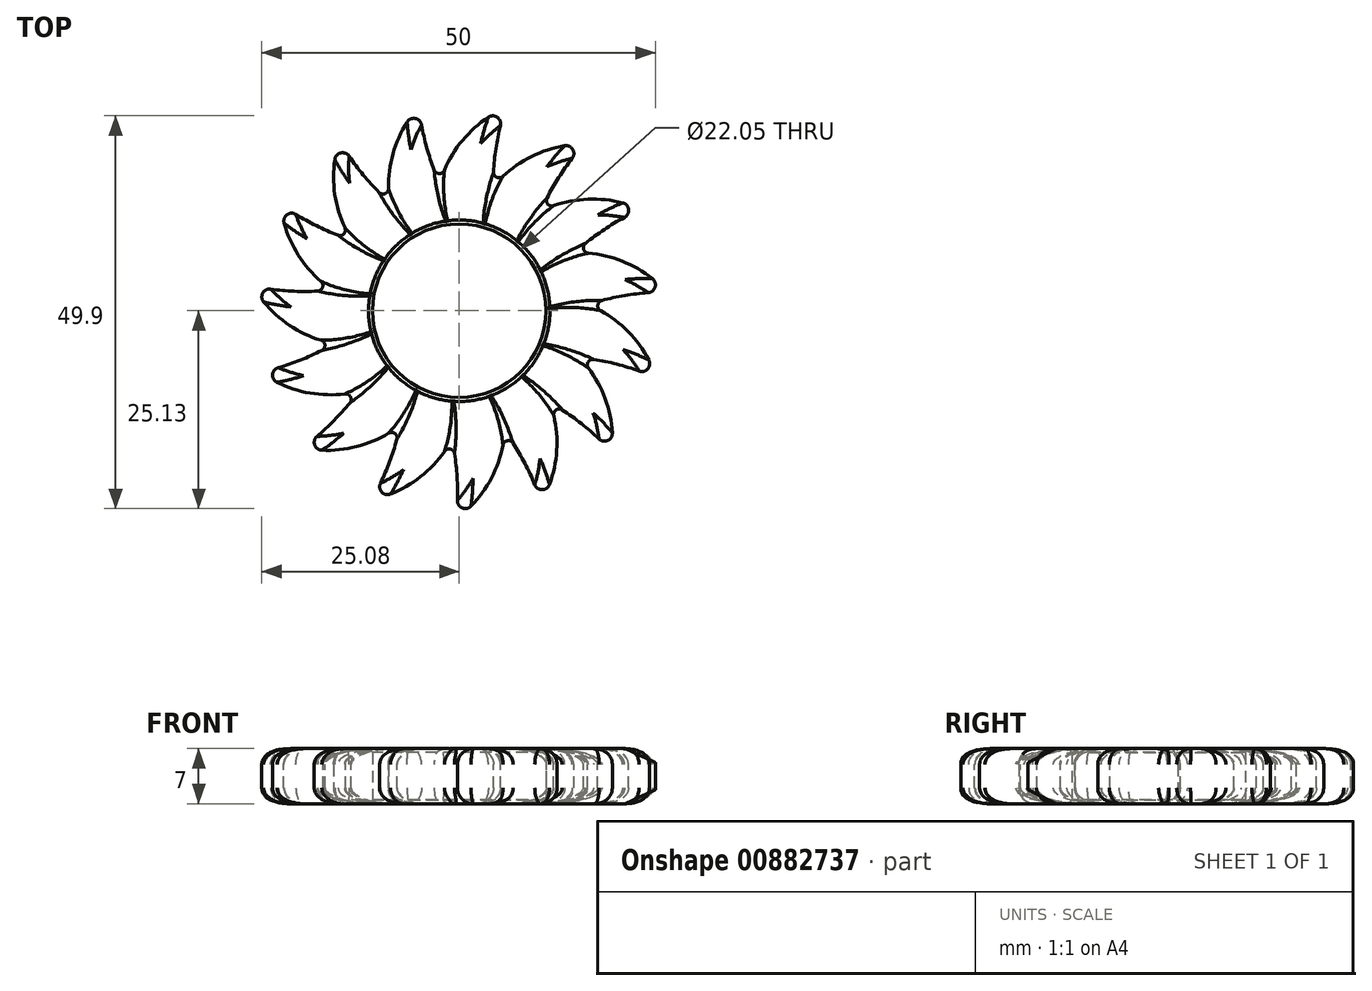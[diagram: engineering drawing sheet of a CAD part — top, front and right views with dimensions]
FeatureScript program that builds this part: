
annotation { "Feature Type Name" : "Feature", "Feature Type Description" : "" }
export const myFeature = defineFeature(function(context is Context, id is Id, definition is map)
    precondition{}
    {
        {
            var Q0;
            Q0=qCreatedBy(makeId("Top.planeOp"),FACE);
            var sketch = newSketch(context, id + "F0", { "sketchPlane" : qUnion([Q0])});
            skCircle(sketch, "E0", {"center": v(0, 0) * mm, "radius": 11.03 * mm});
            skCircle(sketch, "E1", {"center": v(0, 0) * mm, "radius": 14.02 * mm});
            skArc(sketch, "E2", {"start": v(-5.12, 25.95) * mm, "mid": v(-8.64, 19.05) * mm, "end": v(-8.3, 11.3) * mm});
            skArc(sketch, "E3", {"start": v(-5.12, 25.95) * mm, "mid": v(-3.84, 19.77) * mm, "end": v(-1.38, 13.96) * mm});
            skLineSegment(sketch, "E4", {"start": v(-5.12, 25.95) * mm, "end": v(-3.79, 13.5) * mm});
            skSolve(sketch);
        }
        {
            var Q0;
            Q0=qCreatedBy(makeId("Right.planeOp"),FACE);
            var sketch = newSketch(context, id + "F1", { "sketchPlane" : qUnion([Q0])});
            skLineSegment(sketch, "E5", {"start": v(0, 0) * mm, "end": v(0, 14.37) * mm});
            skSolve(sketch);
        }
        {
            var Q0;
            {var subQ0=sQuery(id+"F0.wireOp",EDGE,"E2");Q0=makeQuery(id+"F0.imprint","IMPRINT",FACE,{"disambiguationData":[TD([[makeQuery(id+"F0.imprint","IMPRINT",EDGE,{"derivedFrom":subQ0}),1.0]])]});}
            var Q1;
            Q1=makeQuery(id+"F0.imprint","IMPRINT",FACE,{"disambiguationData":[TD([[makeQuery(id+"F0.imprint","IMPRINT",EDGE,{"derivedFrom":sQuery(id+"F0.wireOp",EDGE,"E0")}),-1.0]])]});
            var Q2;
            {var subQ0=sQuery(id+"F0.wireOp",EDGE,"E3");Q2=makeQuery(id+"F0.imprint","IMPRINT",FACE,{"disambiguationData":[TD([[makeQuery(id+"F0.imprint","IMPRINT",EDGE,{"derivedFrom":subQ0}),-1.0]])]});}
            extrude(context, id + "F2", {"entities" : qUnion([Q0, Q1, Q2]), "depth" : 7 * mm, "offsetDistance" : 25 * mm});
        }
        {
            var Q0;
            Q0=makeQuery(id+"F2.opExtrude","SWEPT_EDGE",EDGE,{"disambiguationData":[OSD([sQuery(id+"F0.wireOp",EDGE,"E2"),sQuery(id+"F0.wireOp",EDGE,"E3"),sQuery(id+"F0.wireOp",EDGE,"E4")])]});
            fillet(context, id + "F3", {"entities" : qUnion([Q0]), "radius" : 1 * mm, "tangentPropagation" : true, "allowEdgeOverflow" : false});
        }
        {
            var Q0;
            Q0=makeQuery(id+"F2.opExtrude","SWEPT_BODY",BODY,{"disambiguationData":[OSD([sQuery(id+"F0.wireOp",EDGE,"E0"),sQuery(id+"F0.wireOp",EDGE,"E1"),sQuery(id+"F0.wireOp",EDGE,"E2"),sQuery(id+"F0.wireOp",EDGE,"E3")])]});
            var Q1;
            Q1=sQuery(id+"F1.wireOp",EDGE,"E5");
            circularPattern(context, id + "F4", {"operationType" : NewBodyOperationType.ADD, "entities" : qUnion([Q0]), "axis" : qUnion([Q1]), "angle" : 360 * degree, "instanceCount" : 15, "equalSpace" : true});
        }
        {
            var Q0;
            Q0=makeQuery(id+"F2.opExtrude","CAP_EDGE",EDGE,{"disambiguationData":[OSD([sQuery(id+"F0.wireOp",EDGE,"E0")])],"isStart":false});
            var Q1;
            Q1=makeQuery(id+"F2.opExtrude","CAP_EDGE",EDGE,{"disambiguationData":[OSD([sQuery(id+"F0.wireOp",EDGE,"E0")])],"isStart":true});
            chamfer(context, id + "F5", {"entities" : qUnion([Q0, Q1]), "width" : .5 * mm, "tangentPropagation" : true});
        }
        {
            var Q0;
            Q0=makeQuery(id+"F4.opPattern","COPY",EDGE,{"derivedFrom":makeQuery(id+"F2.opExtrude","CAP_EDGE",EDGE,{"disambiguationData":[OSD([sQuery(id+"F0.wireOp",EDGE,"E3")])],"isStart":false}),"instanceName":"2"});
            var Q1;
            Q1=makeQuery(id+"F4.opPattern","COPY",EDGE,{"derivedFrom":makeQuery(id+"F2.opExtrude","CAP_EDGE",EDGE,{"disambiguationData":[OSD([sQuery(id+"F0.wireOp",EDGE,"E2")])],"isStart":false}),"instanceName":"1"});
            var Q2;
            Q2=makeQuery(id+"F2.opExtrude","CAP_EDGE",EDGE,{"disambiguationData":[OSD([sQuery(id+"F0.wireOp",EDGE,"E2")])],"isStart":false});
            var Q3;
            Q3=makeQuery(id+"F4.opPattern","COPY",EDGE,{"derivedFrom":makeQuery(id+"F2.opExtrude","CAP_EDGE",EDGE,{"disambiguationData":[OSD([sQuery(id+"F0.wireOp",EDGE,"E2")])],"isStart":false}),"instanceName":"14"});
            var Q4;
            Q4=makeQuery(id+"F4.opPattern","COPY",EDGE,{"derivedFrom":makeQuery(id+"F2.opExtrude","CAP_EDGE",EDGE,{"disambiguationData":[OSD([sQuery(id+"F0.wireOp",EDGE,"E2")])],"isStart":false}),"instanceName":"13"});
            var Q5;
            Q5=makeQuery(id+"F4.opPattern","COPY",EDGE,{"derivedFrom":makeQuery(id+"F2.opExtrude","CAP_EDGE",EDGE,{"disambiguationData":[OSD([sQuery(id+"F0.wireOp",EDGE,"E2")])],"isStart":false}),"instanceName":"12"});
            var Q6;
            Q6=makeQuery(id+"F4.opPattern","COPY",EDGE,{"derivedFrom":makeQuery(id+"F2.opExtrude","CAP_EDGE",EDGE,{"disambiguationData":[OSD([sQuery(id+"F0.wireOp",EDGE,"E2")])],"isStart":false}),"instanceName":"11"});
            var Q7;
            Q7=makeQuery(id+"F4.opPattern","COPY",EDGE,{"derivedFrom":makeQuery(id+"F2.opExtrude","CAP_EDGE",EDGE,{"disambiguationData":[OSD([sQuery(id+"F0.wireOp",EDGE,"E2")])],"isStart":false}),"instanceName":"10"});
            var Q8;
            Q8=makeQuery(id+"F4.opPattern","COPY",EDGE,{"derivedFrom":makeQuery(id+"F2.opExtrude","CAP_EDGE",EDGE,{"disambiguationData":[OSD([sQuery(id+"F0.wireOp",EDGE,"E2")])],"isStart":false}),"instanceName":"9"});
            var Q9;
            Q9=makeQuery(id+"F4.opPattern","COPY",EDGE,{"derivedFrom":makeQuery(id+"F2.opExtrude","CAP_EDGE",EDGE,{"disambiguationData":[OSD([sQuery(id+"F0.wireOp",EDGE,"E2")])],"isStart":false}),"instanceName":"8"});
            var Q10;
            Q10=makeQuery(id+"F4.opPattern","COPY",EDGE,{"derivedFrom":makeQuery(id+"F2.opExtrude","CAP_EDGE",EDGE,{"disambiguationData":[OSD([sQuery(id+"F0.wireOp",EDGE,"E2")])],"isStart":false}),"instanceName":"7"});
            var Q11;
            Q11=makeQuery(id+"F4.opPattern","COPY",EDGE,{"derivedFrom":makeQuery(id+"F2.opExtrude","CAP_EDGE",EDGE,{"disambiguationData":[OSD([sQuery(id+"F0.wireOp",EDGE,"E2")])],"isStart":false}),"instanceName":"6"});
            var Q12;
            Q12=makeQuery(id+"F4.opPattern","COPY",EDGE,{"derivedFrom":makeQuery(id+"F2.opExtrude","CAP_EDGE",EDGE,{"disambiguationData":[OSD([sQuery(id+"F0.wireOp",EDGE,"E2")])],"isStart":false}),"instanceName":"5"});
            var Q13;
            Q13=makeQuery(id+"F4.opPattern","COPY",EDGE,{"derivedFrom":makeQuery(id+"F2.opExtrude","CAP_EDGE",EDGE,{"disambiguationData":[OSD([sQuery(id+"F0.wireOp",EDGE,"E2")])],"isStart":false}),"instanceName":"4"});
            var Q14;
            Q14=makeQuery(id+"F4.opPattern","COPY",EDGE,{"derivedFrom":makeQuery(id+"F2.opExtrude","CAP_EDGE",EDGE,{"disambiguationData":[OSD([sQuery(id+"F0.wireOp",EDGE,"E2")])],"isStart":false}),"instanceName":"3"});
            fillet(context, id + "F6", {"entities" : qUnion([Q0, Q1, Q2, Q3, Q4, Q5, Q6, Q7, Q8, Q9, Q10, Q11, Q12, Q13, Q14]), "radius" : 2 * mm, "tangentPropagation" : true, "allowEdgeOverflow" : false});
        }
        {
            var Q0;
            Q0=makeQuery(id+"F4.opPattern","COPY",EDGE,{"derivedFrom":makeQuery(id+"F2.opExtrude","CAP_EDGE",EDGE,{"disambiguationData":[OSD([sQuery(id+"F0.wireOp",EDGE,"E2")])],"isStart":true}),"instanceName":"1"});
            var Q1;
            Q1=makeQuery(id+"F4.opPattern","COPY",EDGE,{"derivedFrom":makeQuery(id+"F2.opExtrude","CAP_EDGE",EDGE,{"disambiguationData":[OSD([sQuery(id+"F0.wireOp",EDGE,"E2")])],"isStart":true}),"instanceName":"2"});
            var Q2;
            Q2=makeQuery(id+"F4.opPattern","COPY",EDGE,{"derivedFrom":makeQuery(id+"F2.opExtrude","CAP_EDGE",EDGE,{"disambiguationData":[OSD([sQuery(id+"F0.wireOp",EDGE,"E2")])],"isStart":true}),"instanceName":"3"});
            var Q3;
            Q3=makeQuery(id+"F4.opPattern","COPY",EDGE,{"derivedFrom":makeQuery(id+"F2.opExtrude","CAP_EDGE",EDGE,{"disambiguationData":[OSD([sQuery(id+"F0.wireOp",EDGE,"E2")])],"isStart":true}),"instanceName":"4"});
            var Q4;
            Q4=makeQuery(id+"F4.opPattern","COPY",EDGE,{"derivedFrom":makeQuery(id+"F2.opExtrude","CAP_EDGE",EDGE,{"disambiguationData":[OSD([sQuery(id+"F0.wireOp",EDGE,"E2")])],"isStart":true}),"instanceName":"5"});
            var Q5;
            Q5=makeQuery(id+"F4.opPattern","COPY",EDGE,{"derivedFrom":makeQuery(id+"F2.opExtrude","CAP_EDGE",EDGE,{"disambiguationData":[OSD([sQuery(id+"F0.wireOp",EDGE,"E2")])],"isStart":true}),"instanceName":"6"});
            var Q6;
            Q6=makeQuery(id+"F4.opPattern","COPY",EDGE,{"derivedFrom":makeQuery(id+"F2.opExtrude","CAP_EDGE",EDGE,{"disambiguationData":[OSD([sQuery(id+"F0.wireOp",EDGE,"E2")])],"isStart":true}),"instanceName":"7"});
            var Q7;
            Q7=makeQuery(id+"F4.opPattern","COPY",EDGE,{"derivedFrom":makeQuery(id+"F2.opExtrude","CAP_EDGE",EDGE,{"disambiguationData":[OSD([sQuery(id+"F0.wireOp",EDGE,"E2")])],"isStart":true}),"instanceName":"8"});
            var Q8;
            Q8=makeQuery(id+"F4.opPattern","COPY",EDGE,{"derivedFrom":makeQuery(id+"F2.opExtrude","CAP_EDGE",EDGE,{"disambiguationData":[OSD([sQuery(id+"F0.wireOp",EDGE,"E2")])],"isStart":true}),"instanceName":"9"});
            var Q9;
            Q9=makeQuery(id+"F4.opPattern","COPY",EDGE,{"derivedFrom":makeQuery(id+"F2.opExtrude","CAP_EDGE",EDGE,{"disambiguationData":[OSD([sQuery(id+"F0.wireOp",EDGE,"E2")])],"isStart":true}),"instanceName":"10"});
            var Q10;
            Q10=makeQuery(id+"F4.opPattern","COPY",EDGE,{"derivedFrom":makeQuery(id+"F2.opExtrude","CAP_EDGE",EDGE,{"disambiguationData":[OSD([sQuery(id+"F0.wireOp",EDGE,"E2")])],"isStart":true}),"instanceName":"11"});
            var Q11;
            Q11=makeQuery(id+"F4.opPattern","COPY",EDGE,{"derivedFrom":makeQuery(id+"F2.opExtrude","CAP_EDGE",EDGE,{"disambiguationData":[OSD([sQuery(id+"F0.wireOp",EDGE,"E2")])],"isStart":true}),"instanceName":"12"});
            var Q12;
            Q12=makeQuery(id+"F4.opPattern","COPY",EDGE,{"derivedFrom":makeQuery(id+"F2.opExtrude","CAP_EDGE",EDGE,{"disambiguationData":[OSD([sQuery(id+"F0.wireOp",EDGE,"E2")])],"isStart":true}),"instanceName":"13"});
            var Q13;
            Q13=makeQuery(id+"F4.opPattern","COPY",EDGE,{"derivedFrom":makeQuery(id+"F2.opExtrude","CAP_EDGE",EDGE,{"disambiguationData":[OSD([sQuery(id+"F0.wireOp",EDGE,"E2")])],"isStart":true}),"instanceName":"14"});
            var Q14;
            Q14=makeQuery(id+"F2.opExtrude","CAP_EDGE",EDGE,{"disambiguationData":[OSD([sQuery(id+"F0.wireOp",EDGE,"E2")])],"isStart":true});
            fillet(context, id + "F7", {"entities" : qUnion([Q0, Q1, Q2, Q3, Q4, Q5, Q6, Q7, Q8, Q9, Q10, Q11, Q12, Q13, Q14]), "radius" : 2 * mm, "tangentPropagation" : true, "allowEdgeOverflow" : false});
        }
        {
            var Q0;
            Q0=makeQuery(id+"F7.opFillet","BLEND_EDGE",EDGE,{"blendedFrom":[makeQuery(id+"F4.opPattern","COPY",EDGE,{"derivedFrom":makeQuery(id+"F2.opExtrude","CAP_EDGE",EDGE,{"disambiguationData":[OSD([sQuery(id+"F0.wireOp",EDGE,"E2")])],"isStart":true}),"instanceName":"12"}),makeQuery(id+"F4.opPattern","COPY",EDGE,{"derivedFrom":makeQuery(id+"F2.opExtrude","CAP_EDGE",EDGE,{"disambiguationData":[OSD([sQuery(id+"F0.wireOp",EDGE,"E3")])],"isStart":true}),"instanceName":"13"})],"blendedInto":[]});
            var Q1;
            Q1=makeQuery(id+"F7.opFillet","BLEND_EDGE",EDGE,{"blendedFrom":[makeQuery(id+"F4.opPattern","COPY",EDGE,{"derivedFrom":makeQuery(id+"F2.opExtrude","CAP_EDGE",EDGE,{"disambiguationData":[OSD([sQuery(id+"F0.wireOp",EDGE,"E2")])],"isStart":true}),"instanceName":"13"}),makeQuery(id+"F4.opPattern","COPY",EDGE,{"derivedFrom":makeQuery(id+"F2.opExtrude","CAP_EDGE",EDGE,{"disambiguationData":[OSD([sQuery(id+"F0.wireOp",EDGE,"E3")])],"isStart":true}),"instanceName":"14"})],"blendedInto":[]});
            var Q2;
            Q2=makeQuery(id+"F7.opFillet","BLEND_EDGE",EDGE,{"blendedFrom":[makeQuery(id+"F2.opExtrude","CAP_EDGE",EDGE,{"disambiguationData":[OSD([sQuery(id+"F0.wireOp",EDGE,"E3")])],"isStart":true}),makeQuery(id+"F4.opPattern","COPY",EDGE,{"derivedFrom":makeQuery(id+"F2.opExtrude","CAP_EDGE",EDGE,{"disambiguationData":[OSD([sQuery(id+"F0.wireOp",EDGE,"E2")])],"isStart":true}),"instanceName":"14"})],"blendedInto":[]});
            var Q3;
            Q3=makeQuery(id+"F7.opFillet","BLEND_EDGE",EDGE,{"blendedFrom":[makeQuery(id+"F2.opExtrude","CAP_EDGE",EDGE,{"disambiguationData":[OSD([sQuery(id+"F0.wireOp",EDGE,"E2")])],"isStart":true}),makeQuery(id+"F4.opPattern","COPY",EDGE,{"derivedFrom":makeQuery(id+"F2.opExtrude","CAP_EDGE",EDGE,{"disambiguationData":[OSD([sQuery(id+"F0.wireOp",EDGE,"E3")])],"isStart":true}),"instanceName":"1"})],"blendedInto":[]});
            var Q4;
            Q4=makeQuery(id+"F7.opFillet","BLEND_EDGE",EDGE,{"blendedFrom":[makeQuery(id+"F4.opPattern","COPY",EDGE,{"derivedFrom":makeQuery(id+"F2.opExtrude","CAP_EDGE",EDGE,{"disambiguationData":[OSD([sQuery(id+"F0.wireOp",EDGE,"E2")])],"isStart":true}),"instanceName":"1"}),makeQuery(id+"F4.opPattern","COPY",EDGE,{"derivedFrom":makeQuery(id+"F2.opExtrude","CAP_EDGE",EDGE,{"disambiguationData":[OSD([sQuery(id+"F0.wireOp",EDGE,"E3")])],"isStart":true}),"instanceName":"2"})],"blendedInto":[]});
            var Q5;
            Q5=makeQuery(id+"F7.opFillet","BLEND_EDGE",EDGE,{"blendedFrom":[makeQuery(id+"F4.opPattern","COPY",EDGE,{"derivedFrom":makeQuery(id+"F2.opExtrude","CAP_EDGE",EDGE,{"disambiguationData":[OSD([sQuery(id+"F0.wireOp",EDGE,"E2")])],"isStart":true}),"instanceName":"2"}),makeQuery(id+"F4.opPattern","COPY",EDGE,{"derivedFrom":makeQuery(id+"F2.opExtrude","CAP_EDGE",EDGE,{"disambiguationData":[OSD([sQuery(id+"F0.wireOp",EDGE,"E3")])],"isStart":true}),"instanceName":"3"})],"blendedInto":[]});
            var Q6;
            Q6=makeQuery(id+"F7.opFillet","BLEND_EDGE",EDGE,{"blendedFrom":[makeQuery(id+"F4.opPattern","COPY",EDGE,{"derivedFrom":makeQuery(id+"F2.opExtrude","CAP_EDGE",EDGE,{"disambiguationData":[OSD([sQuery(id+"F0.wireOp",EDGE,"E2")])],"isStart":true}),"instanceName":"3"}),makeQuery(id+"F4.opPattern","COPY",EDGE,{"derivedFrom":makeQuery(id+"F2.opExtrude","CAP_EDGE",EDGE,{"disambiguationData":[OSD([sQuery(id+"F0.wireOp",EDGE,"E3")])],"isStart":true}),"instanceName":"4"})],"blendedInto":[]});
            var Q7;
            Q7=makeQuery(id+"F7.opFillet","BLEND_EDGE",EDGE,{"blendedFrom":[makeQuery(id+"F4.opPattern","COPY",EDGE,{"derivedFrom":makeQuery(id+"F2.opExtrude","CAP_EDGE",EDGE,{"disambiguationData":[OSD([sQuery(id+"F0.wireOp",EDGE,"E2")])],"isStart":true}),"instanceName":"4"}),makeQuery(id+"F4.opPattern","COPY",EDGE,{"derivedFrom":makeQuery(id+"F2.opExtrude","CAP_EDGE",EDGE,{"disambiguationData":[OSD([sQuery(id+"F0.wireOp",EDGE,"E3")])],"isStart":true}),"instanceName":"5"})],"blendedInto":[]});
            var Q8;
            Q8=makeQuery(id+"F7.opFillet","BLEND_EDGE",EDGE,{"blendedFrom":[makeQuery(id+"F4.opPattern","COPY",EDGE,{"derivedFrom":makeQuery(id+"F2.opExtrude","CAP_EDGE",EDGE,{"disambiguationData":[OSD([sQuery(id+"F0.wireOp",EDGE,"E2")])],"isStart":true}),"instanceName":"5"}),makeQuery(id+"F4.opPattern","COPY",EDGE,{"derivedFrom":makeQuery(id+"F2.opExtrude","CAP_EDGE",EDGE,{"disambiguationData":[OSD([sQuery(id+"F0.wireOp",EDGE,"E3")])],"isStart":true}),"instanceName":"6"})],"blendedInto":[]});
            var Q9;
            Q9=makeQuery(id+"F7.opFillet","BLEND_EDGE",EDGE,{"blendedFrom":[makeQuery(id+"F4.opPattern","COPY",EDGE,{"derivedFrom":makeQuery(id+"F2.opExtrude","CAP_EDGE",EDGE,{"disambiguationData":[OSD([sQuery(id+"F0.wireOp",EDGE,"E2")])],"isStart":true}),"instanceName":"6"}),makeQuery(id+"F4.opPattern","COPY",EDGE,{"derivedFrom":makeQuery(id+"F2.opExtrude","CAP_EDGE",EDGE,{"disambiguationData":[OSD([sQuery(id+"F0.wireOp",EDGE,"E3")])],"isStart":true}),"instanceName":"7"})],"blendedInto":[]});
            var Q10;
            Q10=makeQuery(id+"F7.opFillet","BLEND_EDGE",EDGE,{"blendedFrom":[makeQuery(id+"F4.opPattern","COPY",EDGE,{"derivedFrom":makeQuery(id+"F2.opExtrude","CAP_EDGE",EDGE,{"disambiguationData":[OSD([sQuery(id+"F0.wireOp",EDGE,"E2")])],"isStart":true}),"instanceName":"7"}),makeQuery(id+"F4.opPattern","COPY",EDGE,{"derivedFrom":makeQuery(id+"F2.opExtrude","CAP_EDGE",EDGE,{"disambiguationData":[OSD([sQuery(id+"F0.wireOp",EDGE,"E3")])],"isStart":true}),"instanceName":"8"})],"blendedInto":[]});
            var Q11;
            Q11=makeQuery(id+"F7.opFillet","BLEND_EDGE",EDGE,{"blendedFrom":[makeQuery(id+"F4.opPattern","COPY",EDGE,{"derivedFrom":makeQuery(id+"F2.opExtrude","CAP_EDGE",EDGE,{"disambiguationData":[OSD([sQuery(id+"F0.wireOp",EDGE,"E2")])],"isStart":true}),"instanceName":"8"}),makeQuery(id+"F4.opPattern","COPY",EDGE,{"derivedFrom":makeQuery(id+"F2.opExtrude","CAP_EDGE",EDGE,{"disambiguationData":[OSD([sQuery(id+"F0.wireOp",EDGE,"E3")])],"isStart":true}),"instanceName":"9"})],"blendedInto":[]});
            var Q12;
            Q12=makeQuery(id+"F7.opFillet","BLEND_EDGE",EDGE,{"blendedFrom":[makeQuery(id+"F4.opPattern","COPY",EDGE,{"derivedFrom":makeQuery(id+"F2.opExtrude","CAP_EDGE",EDGE,{"disambiguationData":[OSD([sQuery(id+"F0.wireOp",EDGE,"E2")])],"isStart":true}),"instanceName":"9"}),makeQuery(id+"F4.opPattern","COPY",EDGE,{"derivedFrom":makeQuery(id+"F2.opExtrude","CAP_EDGE",EDGE,{"disambiguationData":[OSD([sQuery(id+"F0.wireOp",EDGE,"E3")])],"isStart":true}),"instanceName":"10"})],"blendedInto":[]});
            var Q13;
            Q13=makeQuery(id+"F7.opFillet","BLEND_EDGE",EDGE,{"blendedFrom":[makeQuery(id+"F4.opPattern","COPY",EDGE,{"derivedFrom":makeQuery(id+"F2.opExtrude","CAP_EDGE",EDGE,{"disambiguationData":[OSD([sQuery(id+"F0.wireOp",EDGE,"E2")])],"isStart":true}),"instanceName":"10"}),makeQuery(id+"F4.opPattern","COPY",EDGE,{"derivedFrom":makeQuery(id+"F2.opExtrude","CAP_EDGE",EDGE,{"disambiguationData":[OSD([sQuery(id+"F0.wireOp",EDGE,"E3")])],"isStart":true}),"instanceName":"11"})],"blendedInto":[]});
            var Q14;
            Q14=makeQuery(id+"F7.opFillet","BLEND_EDGE",EDGE,{"blendedFrom":[makeQuery(id+"F4.opPattern","COPY",EDGE,{"derivedFrom":makeQuery(id+"F2.opExtrude","CAP_EDGE",EDGE,{"disambiguationData":[OSD([sQuery(id+"F0.wireOp",EDGE,"E2")])],"isStart":true}),"instanceName":"11"}),makeQuery(id+"F4.opPattern","COPY",EDGE,{"derivedFrom":makeQuery(id+"F2.opExtrude","CAP_EDGE",EDGE,{"disambiguationData":[OSD([sQuery(id+"F0.wireOp",EDGE,"E3")])],"isStart":true}),"instanceName":"12"})],"blendedInto":[]});
            fillet(context, id + "F8", {"entities" : qUnion([Q0, Q1, Q2, Q3, Q4, Q5, Q6, Q7, Q8, Q9, Q10, Q11, Q12, Q13, Q14]), "radius" : .7 * mm, "tangentPropagation" : true, "allowEdgeOverflow" : false});
        }
    });
